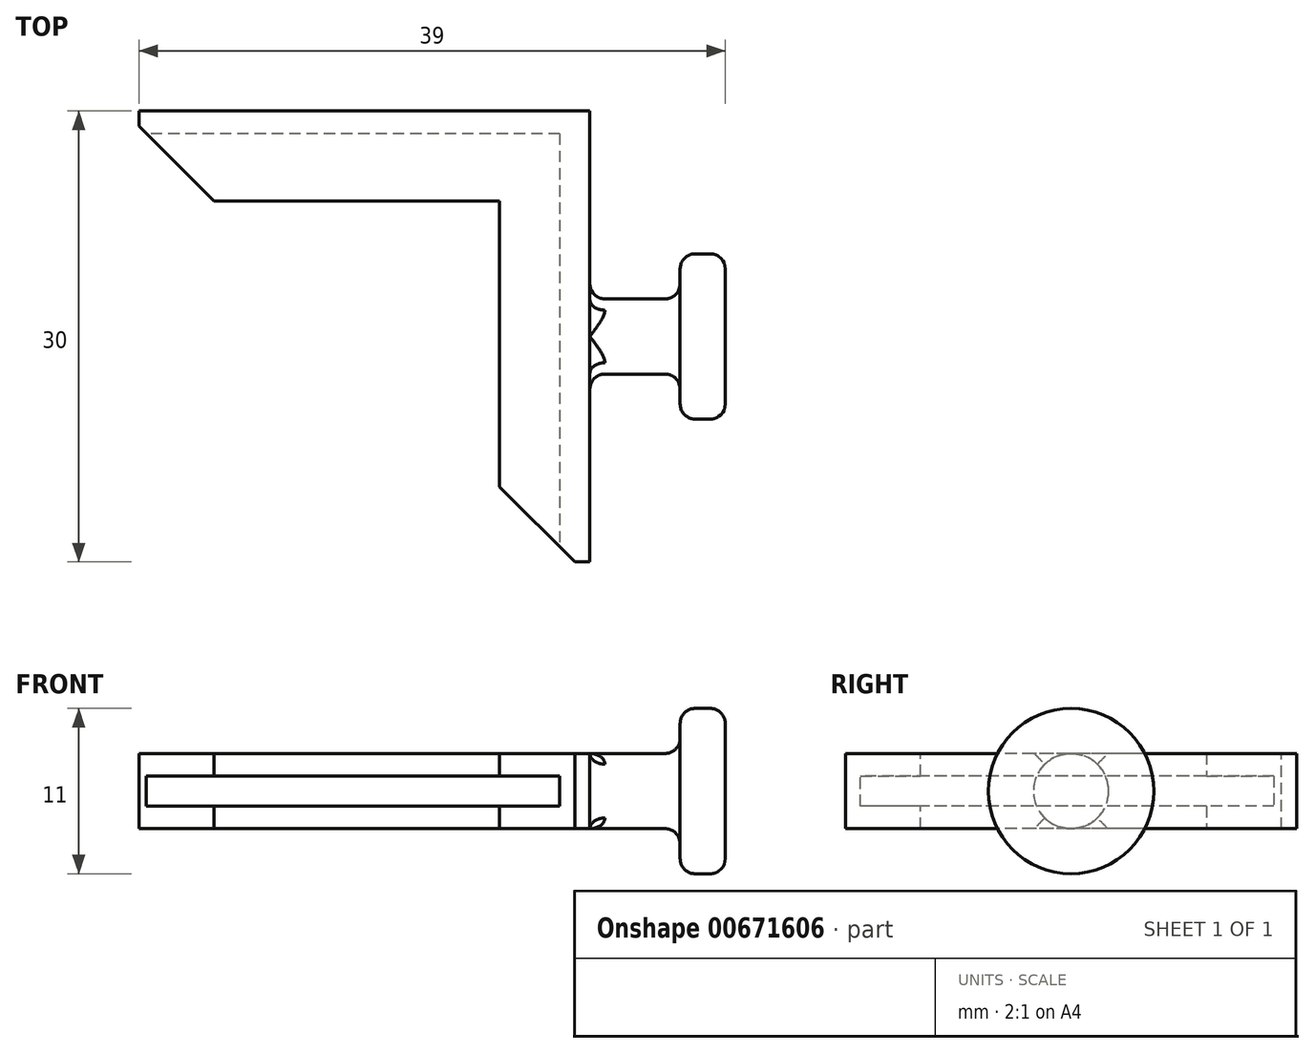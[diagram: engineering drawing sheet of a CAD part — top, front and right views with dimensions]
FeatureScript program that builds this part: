
annotation { "Feature Type Name" : "Feature", "Feature Type Description" : "" }
export const myFeature = defineFeature(function(context is Context, id is Id, definition is map)
    precondition{}
    {
        {
            var Q0;
            Q0=qCreatedBy(makeId("Top.planeOp"),FACE);
            var sketch = newSketch(context, id + "F0", { "sketchPlane" : qUnion([Q0])});
            skLineSegment(sketch, "E0.bottom", {"start": v(15, 15) * mm, "end": v(-15, 15) * mm});
            skLineSegment(sketch, "E0.top", {"start": v(15, -15) * mm, "end": v(9, -15) * mm});
            skLineSegment(sketch, "E0.left", {"start": v(15, 15) * mm, "end": v(15, -15) * mm});
            skLineSegment(sketch, "E0.right", {"start": v(-15, 15) * mm, "end": v(-15, 9) * mm});
            skPoint(sketch, "E0.middle", {"position": v(0, 0) * mm});
            skLineSegment(sketch, "E1.0", {"start": v(9, 9) * mm, "end": v(9, -15) * mm});
            skLineSegment(sketch, "E1.1", {"start": v(9, 9) * mm, "end": v(-15, 9) * mm});
            skLineSegment(sketch, "E2.bottom", {"start": v(15, 2.5) * mm, "end": v(21, 2.5) * mm});
            skLineSegment(sketch, "E2.top", {"start": v(15, 0) * mm, "end": v(24, 0) * mm});
            skLineSegment(sketch, "E2.left", {"start": v(15, 2.5) * mm, "end": v(15, 0) * mm});
            skLineSegment(sketch, "E3.top", {"start": v(21, 5.5) * mm, "end": v(24, 5.5) * mm});
            skLineSegment(sketch, "E3.left", {"start": v(21, 2.5) * mm, "end": v(21, 5.5) * mm});
            skLineSegment(sketch, "E3.right", {"start": v(24, 0) * mm, "end": v(24, 5.5) * mm});
            skSolve(sketch);
        }
        {
            var Q0;
            {var subQ3=sQuery(id+"F0.wireOp",EDGE,"E0.bottom");Q0=makeQuery(id+"F0.imprint","IMPRINT",FACE,{"disambiguationData":[TD([[makeQuery(id+"F0.imprint","IMPRINT",EDGE,{"derivedFrom":subQ3}),1.0]])]});}
            extrude(context, id + "F1", {"entities" : qUnion([Q0]), "endBound" : BoundingType.SYMMETRIC, "depth" : 5 * mm, "offsetDistance" : 25 * mm});
        }
        {
            var Q0;
            Q0=makeQuery(id+"F0.imprint","IMPRINT",FACE,{"disambiguationData":[TD([[makeQuery(id+"F0.imprint","IMPRINT",EDGE,{"derivedFrom":sQuery(id+"F0.wireOp",EDGE,"E2.bottom")}),-1.0]])]});
            var Q1;
            Q1=sQuery(id+"F0.wireOp",EDGE,"E2.top");
            revolve(context, id + "F2", {"operationType" : NewBodyOperationType.ADD, "entities" : qUnion([Q0]), "axis" : qUnion([Q1]), "revolveType" : RevolveType.FULL});
        }
        {
            var Q0;
            Q0=makeQuery(id+"F2.opRevolve","SWEPT_FACE",FACE,{"disambiguationData":[OSD([sQuery(id+"F0.wireOp",EDGE,"E3.right")])]});
            var Q1;
            Q1=makeQuery(id+"F2.opRevolve","SWEPT_EDGE",EDGE,{"disambiguationData":[OSD([sQuery(id+"F0.wireOp",EDGE,"E3.top"),sQuery(id+"F0.wireOp",EDGE,"E3.left")])]});
            fillet(context, id + "F3", {"entities" : qUnion([Q0, Q1]), "radius" : 1 * mm, "tangentPropagation" : true, "allowEdgeOverflow" : false});
        }
        {
            var Q0;
            Q0=makeQuery(id+"F2.opRevolve","SWEPT_EDGE",EDGE,{"disambiguationData":[OSD([sQuery(id+"F0.wireOp",EDGE,"E2.bottom"),sQuery(id+"F0.wireOp",EDGE,"E3.left")])]});
            var Q1;
            Q1=makeQuery(id+"F2.boolean.opBoolean","SPLIT",EDGE,{"disambiguationData":[OD(1.0)],"derivedFrom":makeQuery(id+"F2.opRevolve","SWEPT_EDGE",EDGE,{"disambiguationData":[OSD([sQuery(id+"F0.wireOp",EDGE,"E0.left"),sQuery(id+"F0.wireOp",EDGE,"E2.bottom"),sQuery(id+"F0.wireOp",EDGE,"E2.left")])]})});
            fillet(context, id + "F4", {"entities" : qUnion([Q0, Q1]), "radius" : 1 * mm, "tangentPropagation" : true, "allowEdgeOverflow" : false});
        }
        {
            var Q0;
            Q0=makeQuery(id+"F1.opExtrude","SWEPT_FACE",FACE,{"disambiguationData":[OSD([sQuery(id+"F0.wireOp",EDGE,"E0.right")])]});
            var sketch = newSketch(context, id + "F5", { "sketchPlane" : qUnion([Q0])});
            skLineSegment(sketch, "E4.bottom", {"start": v(-13.5, 1) * mm, "end": v(-9, 1) * mm});
            skLineSegment(sketch, "E4.top", {"start": v(-13.5, -1) * mm, "end": v(-9, -1) * mm});
            skLineSegment(sketch, "E4.left", {"start": v(-13.5, 1) * mm, "end": v(-13.5, -1) * mm});
            skLineSegment(sketch, "E5", {"start": v(-9, -1) * mm, "end": v(-9, 1) * mm});
            skSolve(sketch);
        }
        {
            var Q0;
            Q0=makeQuery(id+"F5.imprint","IMPRINT",FACE,{"disambiguationData":[TD([[makeQuery(id+"F5.imprint","IMPRINT",EDGE,{"derivedFrom":sQuery(id+"F5.wireOp",EDGE,"E4.bottom")}),-1.0]])]});
            extrude(context, id + "F6", {"entities" : qUnion([Q0]), "operationType" : NewBodyOperationType.REMOVE, "oppositeDirection" : true, "depth" : 28 * mm, "offsetDistance" : 25 * mm});
        }
        {
            var Q0;
            Q0=makeQuery(id+"F1.opExtrude","SWEPT_FACE",FACE,{"disambiguationData":[OSD([sQuery(id+"F0.wireOp",EDGE,"E0.top")])]});
            var sketch = newSketch(context, id + "F7", { "sketchPlane" : qUnion([Q0])});
            skLineSegment(sketch, "E6.bottom", {"start": v(13, 1) * mm, "end": v(9, 1) * mm});
            skLineSegment(sketch, "E6.top", {"start": v(13, -1) * mm, "end": v(9, -1) * mm});
            skLineSegment(sketch, "E6.left", {"start": v(13, 1) * mm, "end": v(13, -1) * mm});
            skLineSegment(sketch, "E6.right", {"start": v(9, 1) * mm, "end": v(9, -1) * mm});
            skSolve(sketch);
        }
        {
            var Q0;
            Q0=makeQuery(id+"F7.imprint","IMPRINT",FACE,{"disambiguationData":[TD([[makeQuery(id+"F7.imprint","IMPRINT",EDGE,{"derivedFrom":sQuery(id+"F7.wireOp",EDGE,"E6.bottom")}),1.0]])]});
            extrude(context, id + "F8", {"entities" : qUnion([Q0]), "operationType" : NewBodyOperationType.REMOVE, "oppositeDirection" : true, "depth" : 28.5 * mm, "offsetDistance" : 25 * mm});
        }
        {
            var Q0;
            {var subQ0=sQuery(id+"F0.wireOp",EDGE,"E1.1");var subQ1=sQuery(id+"F0.wireOp",EDGE,"E0.right");Q0=makeQuery(id+"F6.boolean.opBoolean","SPLIT",EDGE,{"disambiguationData":[TD([makeQuery(id+"F6.opExtrude","SWEPT_FACE",FACE,{"disambiguationData":[OSD([sQuery(id+"F5.wireOp",EDGE,"E4.bottom")])]})])],"derivedFrom":makeQuery(id+"F1.opExtrude","SWEPT_EDGE",EDGE,{"disambiguationData":[OSD([subQ1,subQ0])]})});}
            var Q1;
            {var subQ0=sQuery(id+"F0.wireOp",EDGE,"E1.0");var subQ1=sQuery(id+"F0.wireOp",EDGE,"E0.top");Q1=makeQuery(id+"F8.boolean.opBoolean","SPLIT",EDGE,{"disambiguationData":[TD([makeQuery(id+"F6.boolean.opBoolean","COPY",FACE,{"derivedFrom":makeQuery(id+"F6.opExtrude","SWEPT_FACE",FACE,{"disambiguationData":[OSD([sQuery(id+"F5.wireOp",EDGE,"E4.bottom")])]})})])],"derivedFrom":makeQuery(id+"F1.opExtrude","SWEPT_EDGE",EDGE,{"disambiguationData":[OSD([subQ1,subQ0])]})});}
            chamfer(context, id + "F9", {"entities" : qUnion([Q0, Q1]), "width" : 5 * mm, "tangentPropagation" : true});
        }
    });
